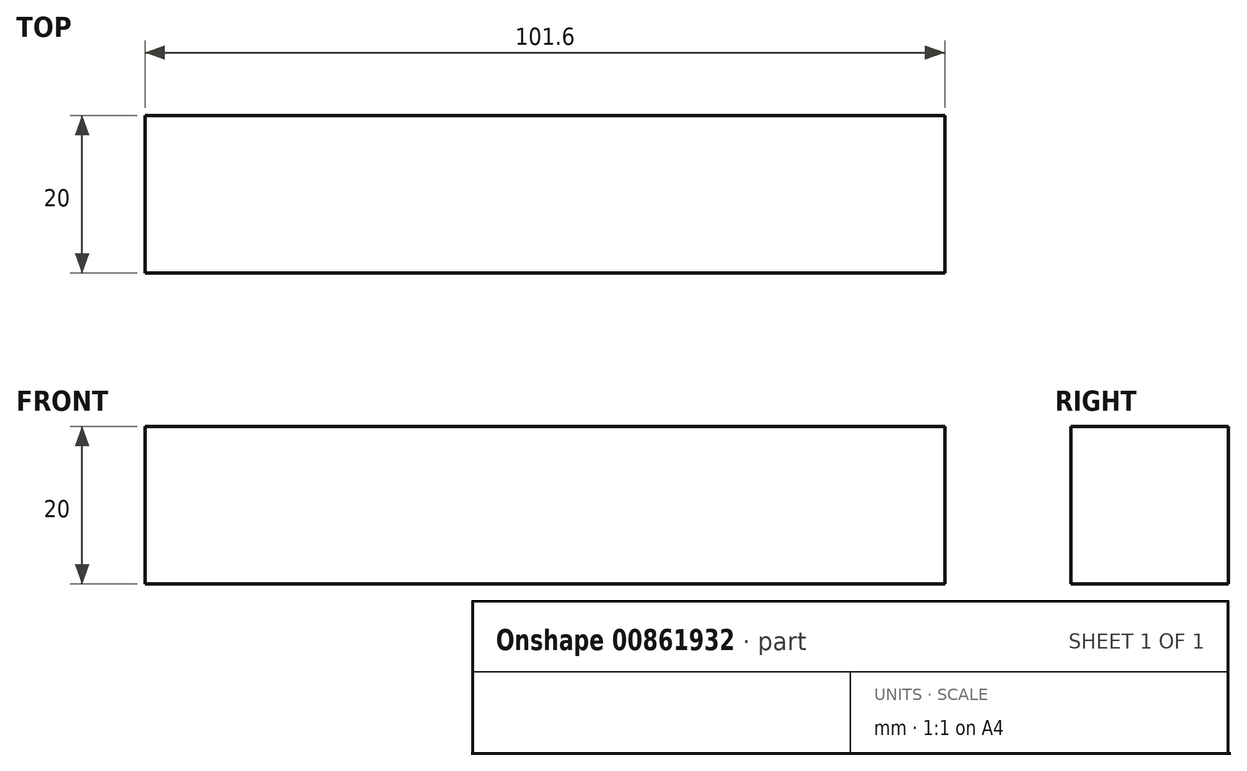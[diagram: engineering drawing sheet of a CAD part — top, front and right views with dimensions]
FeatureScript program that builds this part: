
annotation { "Feature Type Name" : "Feature", "Feature Type Description" : "" }
export const myFeature = defineFeature(function(context is Context, id is Id, definition is map)
    precondition{}
    {
        {
            var Q0;
            Q0=qCreatedBy(makeId("Top.planeOp"),FACE);
            var sketch = newSketch(context, id + "F0", { "sketchPlane" : qUnion([Q0])});
            skLineSegment(sketch, "E0.bottom", {"start": v(-41.2, -20) * mm, "end": v(60.4, -20) * mm});
            skLineSegment(sketch, "E0.top", {"start": v(-41.2, 0) * mm, "end": v(60.4, 0) * mm});
            skLineSegment(sketch, "E0.left", {"start": v(-41.2, -20) * mm, "end": v(-41.2, 0) * mm});
            skLineSegment(sketch, "E0.right", {"start": v(60.4, -20) * mm, "end": v(60.4, 0) * mm});
            skSolve(sketch);
        }
        {
            var Q0;
            Q0 = qSketchRegion(id + "F0", true);
            extrude(context, id + "F1", {"entities" : qUnion([Q0]), "depth" : 20 * mm, "offsetDistance" : 25 * mm});
        }
    });
